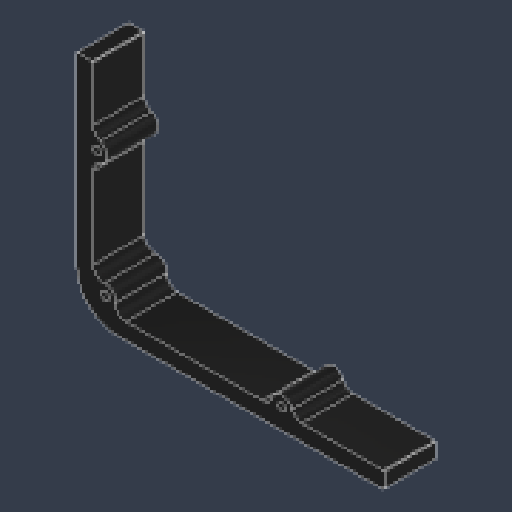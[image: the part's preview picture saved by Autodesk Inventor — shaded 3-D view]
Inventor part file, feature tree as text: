
AUTODESK INVENTOR PART (.ipt)
format: ipt  version: 2023.4 (Build 274418000, 418)  size: 148,480 bytes
history: native  units: mm
features: fillet x4, sketch x3, extrude x2, hole x1
ambient origin geometry x8: Origin, YZ Plane, XZ Plane, XY Plane, X Axis, Y Axis, Z Axis, Center Point
bodies: Solid1 (feature_tree)
feature tree (10):
  extrude  "Extrusion1"  Depth=109.6mm
  fillet  "Fillet1"  Radius=8.0mm
  fillet  "Fillet2"  Radius=8.0mm
  extrude  "Extrusion2"  Depth=25.0mm
  hole  "Hole1"  [1 undecoded]
  fillet  "Fillet3"  Radius=10.0mm
  fillet  "Fillet4"  Radius=14.0mm
  sketch  "Sketch1"  dims[d0=149.6mm d1=109.6mm d2=8.0mm d3=8.0mm]
  sketch  "Sketch2"  dims[d4=25.0mm d5=0.0mm d6=12.0mm]
  sketch  "Sketch3"  dims[d7=20.0mm d8=10.0mm d9=10.0mm d10=14.0mm d11=14.0mm d12=73.0mm d13=100.0mm d14=10.0mm d15=25.0mm d16=0.0mm d17=4.0mm d18=6.0mm d19=7.5mm d20=2.0mm d21=90.0deg d22=15.0mm d23=0.0mm d24=5.0mm d25=0.4mm]
note: 1 required parameter value undecoded (feature->parameter linkage not recoverable at this tier; creation-order binding heuristic only, values carry confidence <= 0.55)
